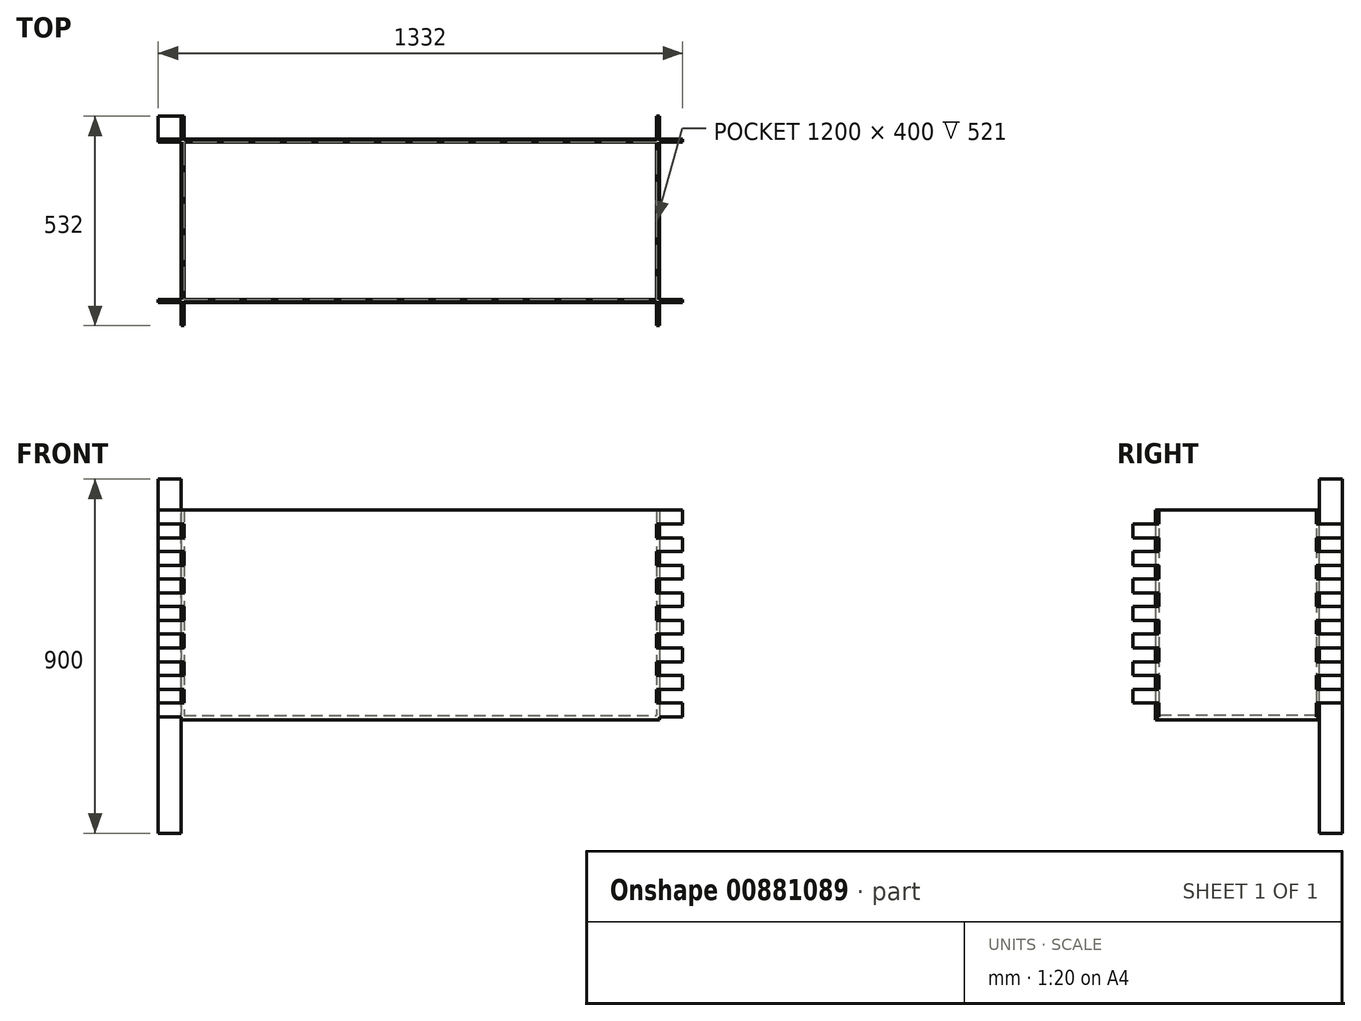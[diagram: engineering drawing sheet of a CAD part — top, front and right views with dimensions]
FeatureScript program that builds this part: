
annotation { "Feature Type Name" : "Feature", "Feature Type Description" : "" }
export const myFeature = defineFeature(function(context is Context, id is Id, definition is map)
    precondition{}
    {
        {
            var Q0;
            Q0=qCreatedBy(makeId("Front.planeOp"),FACE);
            var sketch = newSketch(context, id + "F0", { "sketchPlane" : qUnion([Q0])});
            skLineSegment(sketch, "E0.bottom", {"start": v(-600, 262.5) * mm, "end": v(600, 262.5) * mm});
            skLineSegment(sketch, "E0.top", {"start": v(-600, -262.5) * mm, "end": v(600, -262.5) * mm});
            skLineSegment(sketch, "E0.left", {"start": v(-600, 227.5) * mm, "end": v(-600, 192.5) * mm});
            skPoint(sketch, "E0.middle", {"position": v(0, 0) * mm});
            skLineSegment(sketch, "E1.bottom", {"start": v(-600, 262.5) * mm, "end": v(-666, 262.5) * mm});
            skLineSegment(sketch, "E1.top", {"start": v(-600, 227.5) * mm, "end": v(-666, 227.5) * mm});
            skLineSegment(sketch, "E1.left", {"start": v(-600, 262.5) * mm, "end": v(-600, 227.5) * mm, "construction": true});
            skLineSegment(sketch, "E1.right", {"start": v(-666, 262.5) * mm, "end": v(-666, 227.5) * mm});
            skLineSegment(sketch, "E2.0.1.0", {"start": v(-666, 192.5) * mm, "end": v(-666, 157.5) * mm});
            skLineSegment(sketch, "E2.0.1.1", {"start": v(-600, 192.5) * mm, "end": v(-666, 192.5) * mm});
            skLineSegment(sketch, "E2.0.1.2", {"start": v(-600, 157.5) * mm, "end": v(-666, 157.5) * mm});
            skLineSegment(sketch, "E2.0.2.0", {"start": v(-666, 122.5) * mm, "end": v(-666, 87.5) * mm});
            skLineSegment(sketch, "E2.0.2.1", {"start": v(-600, 122.5) * mm, "end": v(-666, 122.5) * mm});
            skLineSegment(sketch, "E2.0.2.2", {"start": v(-600, 87.5) * mm, "end": v(-666, 87.5) * mm});
            skLineSegment(sketch, "E2.0.3.0", {"start": v(-666, 52.5) * mm, "end": v(-666, 17.5) * mm});
            skLineSegment(sketch, "E2.0.3.1", {"start": v(-600, 52.5) * mm, "end": v(-666, 52.5) * mm});
            skLineSegment(sketch, "E2.0.3.2", {"start": v(-600, 17.5) * mm, "end": v(-666, 17.5) * mm});
            skLineSegment(sketch, "E2.direction1", {"start": v(-666, 227.5) * mm, "end": v(-600, 227.5) * mm, "construction": true});
            skLineSegment(sketch, "E2.direction2", {"start": v(-666, 227.5) * mm, "end": v(-666, 157.5) * mm, "construction": true});
            skLineSegment(sketch, "E3.trimOffspring", {"start": v(-600, 87.5) * mm, "end": v(-600, 52.5) * mm});
            skLineSegment(sketch, "E4.trimOffspring", {"start": v(-600, 157.5) * mm, "end": v(-600, 122.5) * mm});
            skLineSegment(sketch, "E5.0.0.4", {"start": v(-666, -17.5) * mm, "end": v(-666, -52.5) * mm});
            skLineSegment(sketch, "E5.3.0.4", {"start": v(-600, -17.5) * mm, "end": v(-666, -17.5) * mm});
            skLineSegment(sketch, "E5.6.0.4", {"start": v(-600, -52.5) * mm, "end": v(-666, -52.5) * mm});
            skLineSegment(sketch, "E5.0.0.5", {"start": v(-666, -87.5) * mm, "end": v(-666, -122.5) * mm});
            skLineSegment(sketch, "E5.3.0.5", {"start": v(-600, -87.5) * mm, "end": v(-666, -87.5) * mm});
            skLineSegment(sketch, "E5.6.0.5", {"start": v(-600, -122.5) * mm, "end": v(-666, -122.5) * mm});
            skLineSegment(sketch, "E5.0.0.6", {"start": v(-666, -157.5) * mm, "end": v(-666, -192.5) * mm});
            skLineSegment(sketch, "E5.3.0.6", {"start": v(-600, -157.5) * mm, "end": v(-666, -157.5) * mm});
            skLineSegment(sketch, "E5.6.0.6", {"start": v(-600, -192.5) * mm, "end": v(-666, -192.5) * mm});
            skLineSegment(sketch, "E6", {"start": v(-600, 17.5) * mm, "end": v(-600, -17.5) * mm});
            skLineSegment(sketch, "E7", {"start": v(-600, -52.5) * mm, "end": v(-600, -87.5) * mm});
            skLineSegment(sketch, "E8", {"start": v(-600, -122.5) * mm, "end": v(-600, -157.5) * mm});
            skLineSegment(sketch, "E9.MirrorCS", {"start": v(600, -192.5) * mm, "end": v(666, -192.5) * mm});
            skLineSegment(sketch, "E10.MirrorCS", {"start": v(600, 262.5) * mm, "end": v(666, 262.5) * mm});
            skLineSegment(sketch, "E11.MirrorCS", {"start": v(600, 262.5) * mm, "end": v(600, 227.5) * mm, "construction": true});
            skLineSegment(sketch, "E12.MirrorCS", {"start": v(600, 17.5) * mm, "end": v(600, -17.5) * mm});
            skLineSegment(sketch, "E13.MirrorCS", {"start": v(600, 87.5) * mm, "end": v(600, 52.5) * mm});
            skLineSegment(sketch, "E14.MirrorCS", {"start": v(600, -122.5) * mm, "end": v(600, -157.5) * mm});
            skLineSegment(sketch, "E15.MirrorCS", {"start": v(600, 157.5) * mm, "end": v(600, 122.5) * mm});
            skLineSegment(sketch, "E16.MirrorCS", {"start": v(600, 227.5) * mm, "end": v(600, 192.5) * mm});
            skLineSegment(sketch, "E17.MirrorCS", {"start": v(600, -52.5) * mm, "end": v(600, -87.5) * mm});
            skLineSegment(sketch, "E18.MirrorCS", {"start": v(600, 227.5) * mm, "end": v(666, 227.5) * mm});
            skLineSegment(sketch, "E19.MirrorCS", {"start": v(600, -17.5) * mm, "end": v(666, -17.5) * mm});
            skLineSegment(sketch, "E20.MirrorCS", {"start": v(600, 157.5) * mm, "end": v(666, 157.5) * mm});
            skLineSegment(sketch, "E21.MirrorCS", {"start": v(600, 87.5) * mm, "end": v(666, 87.5) * mm});
            skLineSegment(sketch, "E22.MirrorCS", {"start": v(600, 17.5) * mm, "end": v(666, 17.5) * mm});
            skLineSegment(sketch, "E23.MirrorCS", {"start": v(666, 227.5) * mm, "end": v(666, 157.5) * mm, "construction": true});
            skLineSegment(sketch, "E24.MirrorCS", {"start": v(666, 227.5) * mm, "end": v(600, 227.5) * mm, "construction": true});
            skLineSegment(sketch, "E25.MirrorCS", {"start": v(600, -87.5) * mm, "end": v(666, -87.5) * mm});
            skLineSegment(sketch, "E26.MirrorCS", {"start": v(600, -122.5) * mm, "end": v(666, -122.5) * mm});
            skLineSegment(sketch, "E27.MirrorCS", {"start": v(600, -52.5) * mm, "end": v(666, -52.5) * mm});
            skLineSegment(sketch, "E28.MirrorCS", {"start": v(600, 192.5) * mm, "end": v(666, 192.5) * mm});
            skLineSegment(sketch, "E29.MirrorCS", {"start": v(600, 52.5) * mm, "end": v(666, 52.5) * mm});
            skLineSegment(sketch, "E30.MirrorCS", {"start": v(600, -157.5) * mm, "end": v(666, -157.5) * mm});
            skLineSegment(sketch, "E31.MirrorCS", {"start": v(600, 122.5) * mm, "end": v(666, 122.5) * mm});
            skLineSegment(sketch, "E32.MirrorCS", {"start": v(666, -17.5) * mm, "end": v(666, -52.5) * mm});
            skLineSegment(sketch, "E33.MirrorCS", {"start": v(666, -87.5) * mm, "end": v(666, -122.5) * mm});
            skLineSegment(sketch, "E34.MirrorCS", {"start": v(666, 262.5) * mm, "end": v(666, 227.5) * mm});
            skLineSegment(sketch, "E35.MirrorCS", {"start": v(666, 122.5) * mm, "end": v(666, 87.5) * mm});
            skLineSegment(sketch, "E36.MirrorCS", {"start": v(666, 192.5) * mm, "end": v(666, 157.5) * mm});
            skLineSegment(sketch, "E37.MirrorCS", {"start": v(666, -157.5) * mm, "end": v(666, -192.5) * mm});
            skLineSegment(sketch, "E38.MirrorCS", {"start": v(666, 52.5) * mm, "end": v(666, 17.5) * mm});
            skLineSegment(sketch, "E39.0.0.7", {"start": v(-666, -227.5) * mm, "end": v(-666, -262.5) * mm});
            skLineSegment(sketch, "E39.3.0.7", {"start": v(-600, -227.5) * mm, "end": v(-666, -227.5) * mm});
            skLineSegment(sketch, "E39.6.0.7", {"start": v(-600, -262.5) * mm, "end": v(-666, -262.5) * mm});
            skLineSegment(sketch, "E40", {"start": v(-600, -192.5) * mm, "end": v(-600, -227.5) * mm});
            skLineSegment(sketch, "E41.MirrorCS", {"start": v(600, -262.5) * mm, "end": v(666, -262.5) * mm});
            skLineSegment(sketch, "E42.MirrorCS", {"start": v(666, -227.5) * mm, "end": v(666, -262.5) * mm});
            skLineSegment(sketch, "E43.MirrorCS", {"start": v(600, -227.5) * mm, "end": v(666, -227.5) * mm});
            skLineSegment(sketch, "E44.MirrorCS", {"start": v(600, -192.5) * mm, "end": v(600, -227.5) * mm});
            skSolve(sketch);
        }
        {
            var Q0;
            Q0 = qSketchRegion(id + "F0", true);
            extrude(context, id + "F1", {"entities" : qUnion([Q0]), "depth" : 8 * mm, "offsetDistance" : 25 * mm});
        }
        {
            var Q0;
            Q0=makeQuery(id+"F1.opExtrude","SWEPT_FACE",FACE,{"disambiguationData":[OSD([sQuery(id+"F0.wireOp",EDGE,"E0.left")])]});
            var sketch = newSketch(context, id + "F2", { "sketchPlane" : qUnion([Q0])});
            skLineSegment(sketch, "E45.bottom", {"start": v(0, 262.5) * mm, "end": v(-200, 262.5) * mm});
            skLineSegment(sketch, "E45.top", {"start": v(0, -262.5) * mm, "end": v(-200, -262.5) * mm});
            skLineSegment(sketch, "E45.right", {"start": v(-200, 262.5) * mm, "end": v(-200, -262.5) * mm, "construction": true});
            skLineSegment(sketch, "E46.bottom", {"start": v(0, 227.5) * mm, "end": v(66, 227.5) * mm});
            skLineSegment(sketch, "E46.top", {"start": v(0, 192.5) * mm, "end": v(66, 192.5) * mm});
            skLineSegment(sketch, "E46.left", {"start": v(0, 227.5) * mm, "end": v(0, 192.5) * mm, "construction": true});
            skLineSegment(sketch, "E46.right", {"start": v(66, 227.5) * mm, "end": v(66, 192.5) * mm});
            skLineSegment(sketch, "E47.0.1.0", {"start": v(66, 157.5) * mm, "end": v(66, 122.5) * mm});
            skLineSegment(sketch, "E47.0.1.1", {"start": v(0, 157.5) * mm, "end": v(66, 157.5) * mm});
            skLineSegment(sketch, "E47.0.1.2", {"start": v(0, 122.5) * mm, "end": v(66, 122.5) * mm});
            skLineSegment(sketch, "E47.0.2.0", {"start": v(66, 87.5) * mm, "end": v(66, 52.5) * mm});
            skLineSegment(sketch, "E47.0.2.1", {"start": v(0, 87.5) * mm, "end": v(66, 87.5) * mm});
            skLineSegment(sketch, "E47.0.2.2", {"start": v(0, 52.5) * mm, "end": v(66, 52.5) * mm});
            skLineSegment(sketch, "E47.0.3.0", {"start": v(66, 17.5) * mm, "end": v(66, -17.5) * mm});
            skLineSegment(sketch, "E47.0.3.1", {"start": v(0, 17.5) * mm, "end": v(66, 17.5) * mm});
            skLineSegment(sketch, "E47.0.3.2", {"start": v(0, -17.5) * mm, "end": v(66, -17.5) * mm});
            skLineSegment(sketch, "E47.0.4.0", {"start": v(66, -52.5) * mm, "end": v(66, -87.5) * mm});
            skLineSegment(sketch, "E47.0.4.1", {"start": v(0, -52.5) * mm, "end": v(66, -52.5) * mm});
            skLineSegment(sketch, "E47.0.4.2", {"start": v(0, -87.5) * mm, "end": v(66, -87.5) * mm});
            skLineSegment(sketch, "E47.0.5.0", {"start": v(66, -122.5) * mm, "end": v(66, -157.5) * mm});
            skLineSegment(sketch, "E47.0.5.1", {"start": v(0, -122.5) * mm, "end": v(66, -122.5) * mm});
            skLineSegment(sketch, "E47.0.5.2", {"start": v(0, -157.5) * mm, "end": v(66, -157.5) * mm});
            skLineSegment(sketch, "E47.0.6.0", {"start": v(66, -192.5) * mm, "end": v(66, -227.5) * mm});
            skLineSegment(sketch, "E47.0.6.1", {"start": v(0, -192.5) * mm, "end": v(66, -192.5) * mm});
            skLineSegment(sketch, "E47.0.6.2", {"start": v(0, -227.5) * mm, "end": v(66, -227.5) * mm});
            skLineSegment(sketch, "E47.direction1", {"start": v(0, 192.5) * mm, "end": v(25, 192.5) * mm, "construction": true});
            skLineSegment(sketch, "E47.direction2", {"start": v(0, 192.5) * mm, "end": v(0, 157.5) * mm, "construction": true});
            skLineSegment(sketch, "E48.trimOffspring", {"start": v(0, -227.5) * mm, "end": v(0, -262.5) * mm});
            skLineSegment(sketch, "E49.trimOffspring", {"start": v(0, -157.5) * mm, "end": v(0, -192.5) * mm});
            skLineSegment(sketch, "E50.trimOffspring", {"start": v(0, -87.5) * mm, "end": v(0, -122.5) * mm});
            skLineSegment(sketch, "E51.trimOffspring", {"start": v(0, -17.5) * mm, "end": v(0, -52.5) * mm});
            skLineSegment(sketch, "E52.trimOffspring", {"start": v(0, 52.5) * mm, "end": v(0, 17.5) * mm});
            skLineSegment(sketch, "E53.MirrorCS", {"start": v(-400, -17.5) * mm, "end": v(-400, -52.5) * mm});
            skLineSegment(sketch, "E54.MirrorCS", {"start": v(-466, 157.5) * mm, "end": v(-466, 122.5) * mm});
            skLineSegment(sketch, "E55.MirrorCS", {"start": v(-400, 52.5) * mm, "end": v(-400, 17.5) * mm});
            skLineSegment(sketch, "E56.MirrorCS", {"start": v(-400, -157.5) * mm, "end": v(-400, -192.5) * mm});
            skLineSegment(sketch, "E57.MirrorCS", {"start": v(-400, -227.5) * mm, "end": v(-400, -262.5) * mm});
            skLineSegment(sketch, "E58.MirrorCS", {"start": v(-400, -87.5) * mm, "end": v(-400, -122.5) * mm});
            skLineSegment(sketch, "E59.MirrorCS", {"start": v(-466, -52.5) * mm, "end": v(-466, -87.5) * mm});
            skLineSegment(sketch, "E60.MirrorCS", {"start": v(-400, 192.5) * mm, "end": v(-425, 192.5) * mm, "construction": true});
            skLineSegment(sketch, "E61.MirrorCS", {"start": v(-400, 192.5) * mm, "end": v(-400, 157.5) * mm, "construction": true});
            skLineSegment(sketch, "E62.MirrorCS", {"start": v(-466, -122.5) * mm, "end": v(-466, -157.5) * mm});
            skLineSegment(sketch, "E63.MirrorCS", {"start": v(-466, 227.5) * mm, "end": v(-466, 192.5) * mm});
            skLineSegment(sketch, "E64.MirrorCS", {"start": v(-466, 17.5) * mm, "end": v(-466, -17.5) * mm});
            skLineSegment(sketch, "E65.MirrorCS", {"start": v(-400, 227.5) * mm, "end": v(-466, 227.5) * mm});
            skLineSegment(sketch, "E66.MirrorCS", {"start": v(-400, 87.5) * mm, "end": v(-466, 87.5) * mm});
            skLineSegment(sketch, "E67.MirrorCS", {"start": v(-400, -52.5) * mm, "end": v(-466, -52.5) * mm});
            skLineSegment(sketch, "E68.MirrorCS", {"start": v(-400, -157.5) * mm, "end": v(-466, -157.5) * mm});
            skLineSegment(sketch, "E69.MirrorCS", {"start": v(-466, 87.5) * mm, "end": v(-466, 52.5) * mm});
            skLineSegment(sketch, "E70.MirrorCS", {"start": v(-400, -262.5) * mm, "end": v(-200, -262.5) * mm});
            skLineSegment(sketch, "E71.MirrorCS", {"start": v(-400, -122.5) * mm, "end": v(-466, -122.5) * mm});
            skLineSegment(sketch, "E72.MirrorCS", {"start": v(-400, -192.5) * mm, "end": v(-466, -192.5) * mm});
            skLineSegment(sketch, "E73.MirrorCS", {"start": v(-400, 262.5) * mm, "end": v(-200, 262.5) * mm});
            skLineSegment(sketch, "E74.MirrorCS", {"start": v(-400, 192.5) * mm, "end": v(-466, 192.5) * mm});
            skLineSegment(sketch, "E75.MirrorCS", {"start": v(-400, 52.5) * mm, "end": v(-466, 52.5) * mm});
            skLineSegment(sketch, "E76.MirrorCS", {"start": v(-466, -192.5) * mm, "end": v(-466, -227.5) * mm});
            skLineSegment(sketch, "E77.MirrorCS", {"start": v(-400, -227.5) * mm, "end": v(-466, -227.5) * mm});
            skLineSegment(sketch, "E78.MirrorCS", {"start": v(-400, 122.5) * mm, "end": v(-466, 122.5) * mm});
            skLineSegment(sketch, "E79.MirrorCS", {"start": v(-400, 17.5) * mm, "end": v(-466, 17.5) * mm});
            skLineSegment(sketch, "E80.MirrorCS", {"start": v(-400, -87.5) * mm, "end": v(-466, -87.5) * mm});
            skLineSegment(sketch, "E81.MirrorCS", {"start": v(-400, -17.5) * mm, "end": v(-466, -17.5) * mm});
            skLineSegment(sketch, "E82.MirrorCS", {"start": v(-400, 157.5) * mm, "end": v(-466, 157.5) * mm});
            skLineSegment(sketch, "E83", {"start": v(0, 262.5) * mm, "end": v(0, 227.5) * mm});
            skLineSegment(sketch, "E84", {"start": v(-400, 262.5) * mm, "end": v(-400, 227.5) * mm});
            skLineSegment(sketch, "E85", {"start": v(-400, 192.5) * mm, "end": v(-400, 157.5) * mm});
            skLineSegment(sketch, "E86", {"start": v(-400, 122.5) * mm, "end": v(-400, 87.5) * mm});
            skLineSegment(sketch, "E87", {"start": v(0, 192.5) * mm, "end": v(0, 157.5) * mm});
            skLineSegment(sketch, "E88", {"start": v(0, 122.5) * mm, "end": v(0, 87.5) * mm});
            skSolve(sketch);
        }
        {
            var Q0;
            Q0 = qSketchRegion(id + "F2", true);
            extrude(context, id + "F3", {"entities" : qUnion([Q0]), "depth" : 8 * mm, "offsetDistance" : 25 * mm});
        }
        {
            var Q0;
            Q0=makeQuery(id+"F1.opExtrude","SWEPT_BODY",BODY,{"disambiguationData":[OSD([sQuery(id+"F0.wireOp",EDGE,"E0.bottom"),sQuery(id+"F0.wireOp",EDGE,"E0.top"),sQuery(id+"F0.wireOp",EDGE,"E0.left"),sQuery(id+"F0.wireOp",EDGE,"E0.right"),sQuery(id+"F0.wireOp",EDGE,"E1.bottom"),sQuery(id+"F0.wireOp",EDGE,"E1.top"),sQuery(id+"F0.wireOp",EDGE,"E1.right"),sQuery(id+"F0.wireOp",EDGE,"E2.0.1.0"),sQuery(id+"F0.wireOp",EDGE,"E2.0.1.1"),sQuery(id+"F0.wireOp",EDGE,"E2.0.1.2"),sQuery(id+"F0.wireOp",EDGE,"E2.0.2.0"),sQuery(id+"F0.wireOp",EDGE,"E2.0.2.1"),sQuery(id+"F0.wireOp",EDGE,"E2.0.2.2"),sQuery(id+"F0.wireOp",EDGE,"E2.0.3.0"),sQuery(id+"F0.wireOp",EDGE,"E2.0.3.1"),sQuery(id+"F0.wireOp",EDGE,"E2.0.3.2"),sQuery(id+"F0.wireOp",EDGE,"E3.trimOffspring"),sQuery(id+"F0.wireOp",EDGE,"E4.trimOffspring"),sQuery(id+"F0.wireOp",EDGE,"654a2f8d-9041-4c8a-b6f3-2d41a767b8970.MirrorCS"),sQuery(id+"F0.wireOp",EDGE,"654a2f8d-9041-4c8a-b6f3-2d41a767b8973.MirrorCS"),sQuery(id+"F0.wireOp",EDGE,"654a2f8d-9041-4c8a-b6f3-2d41a767b8974.MirrorCS"),sQuery(id+"F0.wireOp",EDGE,"654a2f8d-9041-4c8a-b6f3-2d41a767b8975.MirrorCS"),sQuery(id+"F0.wireOp",EDGE,"654a2f8d-9041-4c8a-b6f3-2d41a767b8976.MirrorCS"),sQuery(id+"F0.wireOp",EDGE,"654a2f8d-9041-4c8a-b6f3-2d41a767b8977.MirrorCS"),sQuery(id+"F0.wireOp",EDGE,"654a2f8d-9041-4c8a-b6f3-2d41a767b8978.MirrorCS"),sQuery(id+"F0.wireOp",EDGE,"654a2f8d-9041-4c8a-b6f3-2d41a767b8979.MirrorCS"),sQuery(id+"F0.wireOp",EDGE,"654a2f8d-9041-4c8a-b6f3-2d41a767b89710.MirrorCS"),sQuery(id+"F0.wireOp",EDGE,"654a2f8d-9041-4c8a-b6f3-2d41a767b89711.MirrorCS"),sQuery(id+"F0.wireOp",EDGE,"654a2f8d-9041-4c8a-b6f3-2d41a767b89712.MirrorCS"),sQuery(id+"F0.wireOp",EDGE,"654a2f8d-9041-4c8a-b6f3-2d41a767b89713.MirrorCS"),sQuery(id+"F0.wireOp",EDGE,"bc8bf7c9-21a7-4010-bfce-5f4c4d057a0e.trimOffspring"),sQuery(id+"F0.wireOp",EDGE,"681b92e8-f1d6-4e1d-b0cf-531c4123ef25.trimOffspring")])]});
            var Q1;
            Q1=makeQuery(id+"F3.opExtrude","CAP_EDGE",EDGE,{"disambiguationData":[OSD([sQuery(id+"F2.wireOp",EDGE,"E45.bottom"),sQuery(id+"F2.wireOp",EDGE,"47e2e538-1496-4ea3-b9ef-a4fa9e4231cb12.MirrorCS")])],"isStart":true});
            var Q2;
            Q2=makeQuery(id+"F3.opExtrude","CAP_EDGE",EDGE,{"disambiguationData":[OSD([sQuery(id+"F2.wireOp",EDGE,"E45.bottom"),sQuery(id+"F2.wireOp",EDGE,"47e2e538-1496-4ea3-b9ef-a4fa9e4231cb12.MirrorCS")])],"isStart":true});
            transform(context, id + "F4", {"entities" : qUnion([Q0]), "transformType" : TransformType.TRANSLATION_DISTANCE, "transformDirection" : qUnion([Q2]), "distance" : 408 * mm, "makeCopy" : true});
        }
        {
            var Q0;
            Q0=makeQuery(id+"F3.opExtrude","SWEPT_BODY",BODY,{"disambiguationData":[OSD([sQuery(id+"F2.wireOp",EDGE,"E45.bottom"),sQuery(id+"F2.wireOp",EDGE,"E45.top"),sQuery(id+"F2.wireOp",EDGE,"E45.left"),sQuery(id+"F2.wireOp",EDGE,"VXF1F787-3TvO-9pyk-sDkr-mCE38lxiraYs.bottom"),sQuery(id+"F2.wireOp",EDGE,"VXF1F787-3TvO-9pyk-sDkr-mCE38lxiraYs.top"),sQuery(id+"F2.wireOp",EDGE,"VXF1F787-3TvO-9pyk-sDkr-mCE38lxiraYs.right"),sQuery(id+"F2.wireOp",EDGE,"92c54758-7377-47f4-830c-e61f3707310f.trimOffspring"),sQuery(id+"F2.wireOp",EDGE,"0bc62775-f8d2-43f3-b865-df8decdc4d50.0.1.0"),sQuery(id+"F2.wireOp",EDGE,"0bc62775-f8d2-43f3-b865-df8decdc4d50.0.1.1"),sQuery(id+"F2.wireOp",EDGE,"0bc62775-f8d2-43f3-b865-df8decdc4d50.0.1.2"),sQuery(id+"F2.wireOp",EDGE,"0bc62775-f8d2-43f3-b865-df8decdc4d50.0.2.0"),sQuery(id+"F2.wireOp",EDGE,"0bc62775-f8d2-43f3-b865-df8decdc4d50.0.2.1"),sQuery(id+"F2.wireOp",EDGE,"0bc62775-f8d2-43f3-b865-df8decdc4d50.0.2.2"),sQuery(id+"F2.wireOp",EDGE,"ff0d782e-37e5-4f16-8f26-1b271ee1eeec.trimOffspring"),sQuery(id+"F2.wireOp",EDGE,"10025bcf-c629-48f1-9c4a-9b3b977cd7b2.trimOffspring"),sQuery(id+"F2.wireOp",EDGE,"47e2e538-1496-4ea3-b9ef-a4fa9e4231cb0.MirrorCS"),sQuery(id+"F2.wireOp",EDGE,"47e2e538-1496-4ea3-b9ef-a4fa9e4231cb1.MirrorCS"),sQuery(id+"F2.wireOp",EDGE,"47e2e538-1496-4ea3-b9ef-a4fa9e4231cb2.MirrorCS"),sQuery(id+"F2.wireOp",EDGE,"47e2e538-1496-4ea3-b9ef-a4fa9e4231cb5.MirrorCS"),sQuery(id+"F2.wireOp",EDGE,"47e2e538-1496-4ea3-b9ef-a4fa9e4231cb6.MirrorCS"),sQuery(id+"F2.wireOp",EDGE,"47e2e538-1496-4ea3-b9ef-a4fa9e4231cb7.MirrorCS"),sQuery(id+"F2.wireOp",EDGE,"47e2e538-1496-4ea3-b9ef-a4fa9e4231cb8.MirrorCS"),sQuery(id+"F2.wireOp",EDGE,"47e2e538-1496-4ea3-b9ef-a4fa9e4231cb9.MirrorCS"),sQuery(id+"F2.wireOp",EDGE,"47e2e538-1496-4ea3-b9ef-a4fa9e4231cb10.MirrorCS"),sQuery(id+"F2.wireOp",EDGE,"47e2e538-1496-4ea3-b9ef-a4fa9e4231cb11.MirrorCS"),sQuery(id+"F2.wireOp",EDGE,"47e2e538-1496-4ea3-b9ef-a4fa9e4231cb12.MirrorCS"),sQuery(id+"F2.wireOp",EDGE,"47e2e538-1496-4ea3-b9ef-a4fa9e4231cb13.MirrorCS"),sQuery(id+"F2.wireOp",EDGE,"47e2e538-1496-4ea3-b9ef-a4fa9e4231cb14.MirrorCS"),sQuery(id+"F2.wireOp",EDGE,"47e2e538-1496-4ea3-b9ef-a4fa9e4231cb15.MirrorCS"),sQuery(id+"F2.wireOp",EDGE,"47e2e538-1496-4ea3-b9ef-a4fa9e4231cb16.MirrorCS")])]});
            var Q1;
            Q1=makeQuery(id+"F4.opPattern","COPY",EDGE,{"derivedFrom":makeQuery(id+"F1.opExtrude","CAP_EDGE",EDGE,{"disambiguationData":[OSD([sQuery(id+"F0.wireOp",EDGE,"E0.bottom"),sQuery(id+"F0.wireOp",EDGE,"E1.bottom"),sQuery(id+"F0.wireOp",EDGE,"654a2f8d-9041-4c8a-b6f3-2d41a767b8978.MirrorCS")])],"isStart":false}),"instanceName":"1"});
            var Q2;
            Q2=makeQuery(id+"F4.opPattern","COPY",EDGE,{"derivedFrom":makeQuery(id+"F1.opExtrude","CAP_EDGE",EDGE,{"disambiguationData":[OSD([sQuery(id+"F0.wireOp",EDGE,"E0.bottom"),sQuery(id+"F0.wireOp",EDGE,"E1.bottom"),sQuery(id+"F0.wireOp",EDGE,"654a2f8d-9041-4c8a-b6f3-2d41a767b8978.MirrorCS")])],"isStart":true}),"instanceName":"1"});
            transform(context, id + "F5", {"entities" : qUnion([Q0]), "transformType" : TransformType.TRANSLATION_DISTANCE, "transformDirection" : qUnion([Q2]), "distance" : 1208 * mm, "makeCopy" : true});
        }
        {
            var Q0;
            Q0=makeQuery(id+"F4.opPattern","COPY",BODY,{"derivedFrom":makeQuery(id+"F1.opExtrude","SWEPT_BODY",BODY,{"disambiguationData":[OSD([sQuery(id+"F0.wireOp",EDGE,"E0.bottom"),sQuery(id+"F0.wireOp",EDGE,"E0.top"),sQuery(id+"F0.wireOp",EDGE,"E0.left"),sQuery(id+"F0.wireOp",EDGE,"E1.bottom"),sQuery(id+"F0.wireOp",EDGE,"E1.top"),sQuery(id+"F0.wireOp",EDGE,"E1.right"),sQuery(id+"F0.wireOp",EDGE,"E2.0.1.0"),sQuery(id+"F0.wireOp",EDGE,"E2.0.1.1"),sQuery(id+"F0.wireOp",EDGE,"E2.0.1.2"),sQuery(id+"F0.wireOp",EDGE,"E2.0.2.0"),sQuery(id+"F0.wireOp",EDGE,"E2.0.2.1"),sQuery(id+"F0.wireOp",EDGE,"E2.0.2.2"),sQuery(id+"F0.wireOp",EDGE,"E2.0.3.0"),sQuery(id+"F0.wireOp",EDGE,"E2.0.3.1"),sQuery(id+"F0.wireOp",EDGE,"E2.0.3.2"),sQuery(id+"F0.wireOp",EDGE,"E3.trimOffspring"),sQuery(id+"F0.wireOp",EDGE,"E4.trimOffspring"),sQuery(id+"F0.wireOp",EDGE,"E5.0.0.4"),sQuery(id+"F0.wireOp",EDGE,"E5.3.0.4"),sQuery(id+"F0.wireOp",EDGE,"E5.6.0.4"),sQuery(id+"F0.wireOp",EDGE,"E5.0.0.5"),sQuery(id+"F0.wireOp",EDGE,"E5.3.0.5"),sQuery(id+"F0.wireOp",EDGE,"E5.6.0.5"),sQuery(id+"F0.wireOp",EDGE,"E5.0.0.6"),sQuery(id+"F0.wireOp",EDGE,"E5.3.0.6"),sQuery(id+"F0.wireOp",EDGE,"E5.6.0.6"),sQuery(id+"F0.wireOp",EDGE,"E6"),sQuery(id+"F0.wireOp",EDGE,"E7"),sQuery(id+"F0.wireOp",EDGE,"E8"),sQuery(id+"F0.wireOp",EDGE,"E9.MirrorCS"),sQuery(id+"F0.wireOp",EDGE,"E10.MirrorCS"),sQuery(id+"F0.wireOp",EDGE,"E12.MirrorCS"),sQuery(id+"F0.wireOp",EDGE,"E13.MirrorCS"),sQuery(id+"F0.wireOp",EDGE,"E14.MirrorCS"),sQuery(id+"F0.wireOp",EDGE,"E15.MirrorCS"),sQuery(id+"F0.wireOp",EDGE,"E16.MirrorCS"),sQuery(id+"F0.wireOp",EDGE,"E17.MirrorCS"),sQuery(id+"F0.wireOp",EDGE,"E18.MirrorCS"),sQuery(id+"F0.wireOp",EDGE,"E19.MirrorCS"),sQuery(id+"F0.wireOp",EDGE,"E20.MirrorCS"),sQuery(id+"F0.wireOp",EDGE,"E21.MirrorCS"),sQuery(id+"F0.wireOp",EDGE,"E22.MirrorCS"),sQuery(id+"F0.wireOp",EDGE,"E25.MirrorCS"),sQuery(id+"F0.wireOp",EDGE,"E26.MirrorCS"),sQuery(id+"F0.wireOp",EDGE,"E27.MirrorCS"),sQuery(id+"F0.wireOp",EDGE,"E28.MirrorCS"),sQuery(id+"F0.wireOp",EDGE,"E29.MirrorCS"),sQuery(id+"F0.wireOp",EDGE,"E30.MirrorCS"),sQuery(id+"F0.wireOp",EDGE,"E31.MirrorCS"),sQuery(id+"F0.wireOp",EDGE,"E32.MirrorCS"),sQuery(id+"F0.wireOp",EDGE,"E33.MirrorCS"),sQuery(id+"F0.wireOp",EDGE,"E34.MirrorCS"),sQuery(id+"F0.wireOp",EDGE,"E35.MirrorCS"),sQuery(id+"F0.wireOp",EDGE,"E36.MirrorCS"),sQuery(id+"F0.wireOp",EDGE,"E37.MirrorCS"),sQuery(id+"F0.wireOp",EDGE,"E38.MirrorCS"),sQuery(id+"F0.wireOp",EDGE,"E39.0.0.7"),sQuery(id+"F0.wireOp",EDGE,"E39.3.0.7"),sQuery(id+"F0.wireOp",EDGE,"E39.6.0.7"),sQuery(id+"F0.wireOp",EDGE,"E40"),sQuery(id+"F0.wireOp",EDGE,"E41.MirrorCS"),sQuery(id+"F0.wireOp",EDGE,"E42.MirrorCS"),sQuery(id+"F0.wireOp",EDGE,"E43.MirrorCS"),sQuery(id+"F0.wireOp",EDGE,"E44.MirrorCS")])]}),"instanceName":"1"});
            deleteBodies(context, id + "F6", {"entities" : qUnion([Q0])});
        }
        {
            var Q0;
            Q0=makeQuery(id+"F5.opPattern","COPY",FACE,{"derivedFrom":makeQuery(id+"F3.opExtrude","SWEPT_FACE",FACE,{"disambiguationData":[OSD([sQuery(id+"F2.wireOp",EDGE,"E84")])]}),"instanceName":"1"});
            var sketch = newSketch(context, id + "F7", { "sketchPlane" : qUnion([Q0])});
            skLineSegment(sketch, "E89.0.0", {"start": v(-666, -262.5) * mm, "end": v(666, -262.5) * mm});
            skLineSegment(sketch, "E89.0.1", {"start": v(666, -262.5) * mm, "end": v(666, -227.5) * mm});
            skLineSegment(sketch, "E89.0.2", {"start": v(666, -227.5) * mm, "end": v(600, -227.5) * mm});
            skLineSegment(sketch, "E89.0.3", {"start": v(600, -227.5) * mm, "end": v(600, -192.5) * mm});
            skLineSegment(sketch, "E89.0.4", {"start": v(600, -192.5) * mm, "end": v(666, -192.5) * mm});
            skLineSegment(sketch, "E89.0.5", {"start": v(666, -192.5) * mm, "end": v(666, -157.5) * mm});
            skLineSegment(sketch, "E89.0.6", {"start": v(666, -157.5) * mm, "end": v(600, -157.5) * mm});
            skLineSegment(sketch, "E89.0.7", {"start": v(600, -157.5) * mm, "end": v(600, -122.5) * mm});
            skLineSegment(sketch, "E89.0.8", {"start": v(600, -122.5) * mm, "end": v(666, -122.5) * mm});
            skLineSegment(sketch, "E89.0.9", {"start": v(666, -122.5) * mm, "end": v(666, -87.5) * mm});
            skLineSegment(sketch, "E89.0.10", {"start": v(666, -87.5) * mm, "end": v(600, -87.5) * mm});
            skLineSegment(sketch, "E89.0.11", {"start": v(600, -87.5) * mm, "end": v(600, -52.5) * mm});
            skLineSegment(sketch, "E89.0.12", {"start": v(600, -52.5) * mm, "end": v(666, -52.5) * mm});
            skLineSegment(sketch, "E89.0.13", {"start": v(666, -52.5) * mm, "end": v(666, -17.5) * mm});
            skLineSegment(sketch, "E89.0.14", {"start": v(666, -17.5) * mm, "end": v(600, -17.5) * mm});
            skLineSegment(sketch, "E89.0.15", {"start": v(600, -17.5) * mm, "end": v(600, 17.5) * mm});
            skLineSegment(sketch, "E89.0.16", {"start": v(600, 17.5) * mm, "end": v(666, 17.5) * mm});
            skLineSegment(sketch, "E89.0.17", {"start": v(666, 17.5) * mm, "end": v(666, 52.5) * mm});
            skLineSegment(sketch, "E89.0.18", {"start": v(666, 52.5) * mm, "end": v(600, 52.5) * mm});
            skLineSegment(sketch, "E89.0.19", {"start": v(600, 52.5) * mm, "end": v(600, 87.5) * mm});
            skLineSegment(sketch, "E89.0.20", {"start": v(600, 87.5) * mm, "end": v(666, 87.5) * mm});
            skLineSegment(sketch, "E89.0.21", {"start": v(666, 87.5) * mm, "end": v(666, 122.5) * mm});
            skLineSegment(sketch, "E89.0.22", {"start": v(666, 122.5) * mm, "end": v(600, 122.5) * mm});
            skLineSegment(sketch, "E89.0.23", {"start": v(600, 122.5) * mm, "end": v(600, 157.5) * mm});
            skLineSegment(sketch, "E89.0.24", {"start": v(600, 157.5) * mm, "end": v(666, 157.5) * mm});
            skLineSegment(sketch, "E89.0.25", {"start": v(666, 157.5) * mm, "end": v(666, 192.5) * mm});
            skLineSegment(sketch, "E89.0.26", {"start": v(666, 192.5) * mm, "end": v(600, 192.5) * mm});
            skLineSegment(sketch, "E89.0.27", {"start": v(600, 192.5) * mm, "end": v(600, 227.5) * mm});
            skLineSegment(sketch, "E89.0.28", {"start": v(600, 227.5) * mm, "end": v(666, 227.5) * mm});
            skLineSegment(sketch, "E89.0.29", {"start": v(666, 227.5) * mm, "end": v(666, 262.5) * mm});
            skLineSegment(sketch, "E89.0.30", {"start": v(666, 262.5) * mm, "end": v(-666, 262.5) * mm});
            skLineSegment(sketch, "E89.0.31", {"start": v(-666, 262.5) * mm, "end": v(-666, 227.5) * mm});
            skLineSegment(sketch, "E89.0.32", {"start": v(-666, 227.5) * mm, "end": v(-600, 227.5) * mm});
            skLineSegment(sketch, "E89.0.33", {"start": v(-600, 227.5) * mm, "end": v(-600, 192.5) * mm});
            skLineSegment(sketch, "E89.0.34", {"start": v(-600, 192.5) * mm, "end": v(-666, 192.5) * mm});
            skLineSegment(sketch, "E89.0.35", {"start": v(-666, 192.5) * mm, "end": v(-666, 157.5) * mm});
            skLineSegment(sketch, "E89.0.36", {"start": v(-666, 157.5) * mm, "end": v(-600, 157.5) * mm});
            skLineSegment(sketch, "E89.0.37", {"start": v(-600, 157.5) * mm, "end": v(-600, 122.5) * mm});
            skLineSegment(sketch, "E89.0.38", {"start": v(-600, 122.5) * mm, "end": v(-666, 122.5) * mm});
            skLineSegment(sketch, "E89.0.39", {"start": v(-666, 122.5) * mm, "end": v(-666, 87.5) * mm});
            skLineSegment(sketch, "E89.0.40", {"start": v(-666, 87.5) * mm, "end": v(-600, 87.5) * mm});
            skLineSegment(sketch, "E89.0.41", {"start": v(-600, 87.5) * mm, "end": v(-600, 52.5) * mm});
            skLineSegment(sketch, "E89.0.42", {"start": v(-600, 52.5) * mm, "end": v(-666, 52.5) * mm});
            skLineSegment(sketch, "E89.0.43", {"start": v(-666, 52.5) * mm, "end": v(-666, 17.5) * mm});
            skLineSegment(sketch, "E89.0.44", {"start": v(-666, 17.5) * mm, "end": v(-600, 17.5) * mm});
            skLineSegment(sketch, "E89.0.45", {"start": v(-600, 17.5) * mm, "end": v(-600, -17.5) * mm});
            skLineSegment(sketch, "E89.0.46", {"start": v(-600, -17.5) * mm, "end": v(-666, -17.5) * mm});
            skLineSegment(sketch, "E89.0.47", {"start": v(-666, -17.5) * mm, "end": v(-666, -52.5) * mm});
            skLineSegment(sketch, "E89.0.48", {"start": v(-666, -52.5) * mm, "end": v(-600, -52.5) * mm});
            skLineSegment(sketch, "E89.0.49", {"start": v(-600, -52.5) * mm, "end": v(-600, -87.5) * mm});
            skLineSegment(sketch, "E89.0.50", {"start": v(-600, -87.5) * mm, "end": v(-666, -87.5) * mm});
            skLineSegment(sketch, "E89.0.51", {"start": v(-666, -87.5) * mm, "end": v(-666, -122.5) * mm});
            skLineSegment(sketch, "E89.0.52", {"start": v(-666, -122.5) * mm, "end": v(-600, -122.5) * mm});
            skLineSegment(sketch, "E89.0.53", {"start": v(-600, -122.5) * mm, "end": v(-600, -157.5) * mm});
            skLineSegment(sketch, "E89.0.54", {"start": v(-600, -157.5) * mm, "end": v(-666, -157.5) * mm});
            skLineSegment(sketch, "E89.0.55", {"start": v(-666, -157.5) * mm, "end": v(-666, -192.5) * mm});
            skLineSegment(sketch, "E89.0.56", {"start": v(-666, -192.5) * mm, "end": v(-600, -192.5) * mm});
            skLineSegment(sketch, "E89.0.57", {"start": v(-600, -192.5) * mm, "end": v(-600, -227.5) * mm});
            skLineSegment(sketch, "E89.0.58", {"start": v(-600, -227.5) * mm, "end": v(-666, -227.5) * mm});
            skLineSegment(sketch, "E89.0.59", {"start": v(-666, -227.5) * mm, "end": v(-666, -262.5) * mm});
            skSolve(sketch);
        }
        {
            var Q0;
            Q0 = qSketchRegion(id + "F7", true);
            extrude(context, id + "F8", {"entities" : qUnion([Q0]), "depth" : 8 * mm, "offsetDistance" : 25 * mm});
        }
        {
            var Q0;
            Q0=makeQuery(id+"F5.opPattern","COPY",BODY,{"derivedFrom":makeQuery(id+"F3.opExtrude","SWEPT_BODY",BODY,{"disambiguationData":[OSD([sQuery(id+"F2.wireOp",EDGE,"E45.bottom"),sQuery(id+"F2.wireOp",EDGE,"E45.top"),sQuery(id+"F2.wireOp",EDGE,"E46.bottom"),sQuery(id+"F2.wireOp",EDGE,"E46.top"),sQuery(id+"F2.wireOp",EDGE,"E46.right"),sQuery(id+"F2.wireOp",EDGE,"E47.0.1.0"),sQuery(id+"F2.wireOp",EDGE,"E47.0.1.1"),sQuery(id+"F2.wireOp",EDGE,"E47.0.1.2"),sQuery(id+"F2.wireOp",EDGE,"E47.0.2.0"),sQuery(id+"F2.wireOp",EDGE,"E47.0.2.1"),sQuery(id+"F2.wireOp",EDGE,"E47.0.2.2"),sQuery(id+"F2.wireOp",EDGE,"E47.0.3.0"),sQuery(id+"F2.wireOp",EDGE,"E47.0.3.1"),sQuery(id+"F2.wireOp",EDGE,"E47.0.3.2"),sQuery(id+"F2.wireOp",EDGE,"E47.0.4.0"),sQuery(id+"F2.wireOp",EDGE,"E47.0.4.1"),sQuery(id+"F2.wireOp",EDGE,"E47.0.4.2"),sQuery(id+"F2.wireOp",EDGE,"E47.0.5.0"),sQuery(id+"F2.wireOp",EDGE,"E47.0.5.1"),sQuery(id+"F2.wireOp",EDGE,"E47.0.5.2"),sQuery(id+"F2.wireOp",EDGE,"E47.0.6.0"),sQuery(id+"F2.wireOp",EDGE,"E47.0.6.1"),sQuery(id+"F2.wireOp",EDGE,"E47.0.6.2"),sQuery(id+"F2.wireOp",EDGE,"E48.trimOffspring"),sQuery(id+"F2.wireOp",EDGE,"E49.trimOffspring"),sQuery(id+"F2.wireOp",EDGE,"E50.trimOffspring"),sQuery(id+"F2.wireOp",EDGE,"E51.trimOffspring"),sQuery(id+"F2.wireOp",EDGE,"E52.trimOffspring"),sQuery(id+"F2.wireOp",EDGE,"E53.MirrorCS"),sQuery(id+"F2.wireOp",EDGE,"E54.MirrorCS"),sQuery(id+"F2.wireOp",EDGE,"E55.MirrorCS"),sQuery(id+"F2.wireOp",EDGE,"E56.MirrorCS"),sQuery(id+"F2.wireOp",EDGE,"E57.MirrorCS"),sQuery(id+"F2.wireOp",EDGE,"E58.MirrorCS"),sQuery(id+"F2.wireOp",EDGE,"E59.MirrorCS"),sQuery(id+"F2.wireOp",EDGE,"E62.MirrorCS"),sQuery(id+"F2.wireOp",EDGE,"E63.MirrorCS"),sQuery(id+"F2.wireOp",EDGE,"E64.MirrorCS"),sQuery(id+"F2.wireOp",EDGE,"E65.MirrorCS"),sQuery(id+"F2.wireOp",EDGE,"E66.MirrorCS"),sQuery(id+"F2.wireOp",EDGE,"E67.MirrorCS"),sQuery(id+"F2.wireOp",EDGE,"E68.MirrorCS"),sQuery(id+"F2.wireOp",EDGE,"E69.MirrorCS"),sQuery(id+"F2.wireOp",EDGE,"E70.MirrorCS"),sQuery(id+"F2.wireOp",EDGE,"E71.MirrorCS"),sQuery(id+"F2.wireOp",EDGE,"E72.MirrorCS"),sQuery(id+"F2.wireOp",EDGE,"E73.MirrorCS"),sQuery(id+"F2.wireOp",EDGE,"E74.MirrorCS"),sQuery(id+"F2.wireOp",EDGE,"E75.MirrorCS"),sQuery(id+"F2.wireOp",EDGE,"E76.MirrorCS"),sQuery(id+"F2.wireOp",EDGE,"E77.MirrorCS"),sQuery(id+"F2.wireOp",EDGE,"E78.MirrorCS"),sQuery(id+"F2.wireOp",EDGE,"E79.MirrorCS"),sQuery(id+"F2.wireOp",EDGE,"E80.MirrorCS"),sQuery(id+"F2.wireOp",EDGE,"E81.MirrorCS"),sQuery(id+"F2.wireOp",EDGE,"E82.MirrorCS"),sQuery(id+"F2.wireOp",EDGE,"E83"),sQuery(id+"F2.wireOp",EDGE,"E84"),sQuery(id+"F2.wireOp",EDGE,"E85"),sQuery(id+"F2.wireOp",EDGE,"E86"),sQuery(id+"F2.wireOp",EDGE,"E87"),sQuery(id+"F2.wireOp",EDGE,"E88")])]}),"instanceName":"1"});
            deleteBodies(context, id + "F9", {"entities" : qUnion([Q0])});
        }
        {
            var Q0;
            Q0=makeQuery(id+"F8.opExtrude","SWEPT_FACE",FACE,{"disambiguationData":[OSD([sQuery(id+"F7.wireOp",EDGE,"E89.0.49")])]});
            var sketch = newSketch(context, id + "F10", { "sketchPlane" : qUnion([Q0])});
            skLineSegment(sketch, "E90.0.0", {"start": v(0, 192.5) * mm, "end": v(0, 157.5) * mm});
            skLineSegment(sketch, "E90.0.1", {"start": v(0, 157.5) * mm, "end": v(-66, 157.5) * mm});
            skLineSegment(sketch, "E90.0.2", {"start": v(-66, 157.5) * mm, "end": v(-66, 122.5) * mm});
            skLineSegment(sketch, "E90.0.3", {"start": v(-66, 122.5) * mm, "end": v(0, 122.5) * mm});
            skLineSegment(sketch, "E90.0.4", {"start": v(0, 122.5) * mm, "end": v(0, 87.5) * mm});
            skLineSegment(sketch, "E90.0.5", {"start": v(0, 87.5) * mm, "end": v(-66, 87.5) * mm});
            skLineSegment(sketch, "E90.0.6", {"start": v(-66, 87.5) * mm, "end": v(-66, 52.5) * mm});
            skLineSegment(sketch, "E90.0.7", {"start": v(-66, 52.5) * mm, "end": v(0, 52.5) * mm});
            skLineSegment(sketch, "E90.0.8", {"start": v(0, 52.5) * mm, "end": v(0, 17.5) * mm});
            skLineSegment(sketch, "E90.0.9", {"start": v(0, 17.5) * mm, "end": v(-66, 17.5) * mm});
            skLineSegment(sketch, "E90.0.10", {"start": v(-66, 17.5) * mm, "end": v(-66, -17.5) * mm});
            skLineSegment(sketch, "E90.0.11", {"start": v(-66, -17.5) * mm, "end": v(0, -17.5) * mm});
            skLineSegment(sketch, "E90.0.12", {"start": v(0, -17.5) * mm, "end": v(0, -52.5) * mm});
            skLineSegment(sketch, "E90.0.13", {"start": v(0, -52.5) * mm, "end": v(-66, -52.5) * mm});
            skLineSegment(sketch, "E90.0.14", {"start": v(-66, -52.5) * mm, "end": v(-66, -87.5) * mm});
            skLineSegment(sketch, "E90.0.15", {"start": v(-66, -87.5) * mm, "end": v(0, -87.5) * mm});
            skLineSegment(sketch, "E90.0.16", {"start": v(0, -87.5) * mm, "end": v(0, -122.5) * mm});
            skLineSegment(sketch, "E90.0.17", {"start": v(0, -122.5) * mm, "end": v(-66, -122.5) * mm});
            skLineSegment(sketch, "E90.0.18", {"start": v(-66, -122.5) * mm, "end": v(-66, -157.5) * mm});
            skLineSegment(sketch, "E90.0.19", {"start": v(-66, -157.5) * mm, "end": v(0, -157.5) * mm});
            skLineSegment(sketch, "E90.0.20", {"start": v(0, -157.5) * mm, "end": v(0, -192.5) * mm});
            skLineSegment(sketch, "E90.0.21", {"start": v(0, -192.5) * mm, "end": v(-66, -192.5) * mm});
            skLineSegment(sketch, "E90.0.22", {"start": v(-66, -192.5) * mm, "end": v(-66, -227.5) * mm});
            skLineSegment(sketch, "E90.0.23", {"start": v(-66, -227.5) * mm, "end": v(0, -227.5) * mm});
            skLineSegment(sketch, "E90.0.24", {"start": v(0, -227.5) * mm, "end": v(0, -262.5) * mm});
            skLineSegment(sketch, "E90.0.25", {"start": v(0, -262.5) * mm, "end": v(400, -262.5) * mm});
            skLineSegment(sketch, "E90.0.26", {"start": v(400, -262.5) * mm, "end": v(400, -227.5) * mm});
            skLineSegment(sketch, "E90.0.27", {"start": v(400, -227.5) * mm, "end": v(466, -227.5) * mm});
            skLineSegment(sketch, "E90.0.28", {"start": v(466, -227.5) * mm, "end": v(466, -192.5) * mm});
            skLineSegment(sketch, "E90.0.29", {"start": v(466, -192.5) * mm, "end": v(400, -192.5) * mm});
            skLineSegment(sketch, "E90.0.30", {"start": v(400, -192.5) * mm, "end": v(400, -157.5) * mm});
            skLineSegment(sketch, "E90.0.31", {"start": v(400, -157.5) * mm, "end": v(466, -157.5) * mm});
            skLineSegment(sketch, "E90.0.32", {"start": v(466, -157.5) * mm, "end": v(466, -122.5) * mm});
            skLineSegment(sketch, "E90.0.33", {"start": v(466, -122.5) * mm, "end": v(400, -122.5) * mm});
            skLineSegment(sketch, "E90.0.34", {"start": v(400, -122.5) * mm, "end": v(400, -87.5) * mm});
            skLineSegment(sketch, "E90.0.35", {"start": v(400, -87.5) * mm, "end": v(466, -87.5) * mm});
            skLineSegment(sketch, "E90.0.36", {"start": v(466, -87.5) * mm, "end": v(466, -52.5) * mm});
            skLineSegment(sketch, "E90.0.37", {"start": v(466, -52.5) * mm, "end": v(400, -52.5) * mm});
            skLineSegment(sketch, "E90.0.38", {"start": v(400, -52.5) * mm, "end": v(400, -17.5) * mm});
            skLineSegment(sketch, "E90.0.39", {"start": v(400, -17.5) * mm, "end": v(466, -17.5) * mm});
            skLineSegment(sketch, "E90.0.40", {"start": v(466, -17.5) * mm, "end": v(466, 17.5) * mm});
            skLineSegment(sketch, "E90.0.41", {"start": v(466, 17.5) * mm, "end": v(400, 17.5) * mm});
            skLineSegment(sketch, "E90.0.42", {"start": v(400, 17.5) * mm, "end": v(400, 52.5) * mm});
            skLineSegment(sketch, "E90.0.43", {"start": v(400, 52.5) * mm, "end": v(466, 52.5) * mm});
            skLineSegment(sketch, "E90.0.44", {"start": v(466, 52.5) * mm, "end": v(466, 87.5) * mm});
            skLineSegment(sketch, "E90.0.45", {"start": v(466, 87.5) * mm, "end": v(400, 87.5) * mm});
            skLineSegment(sketch, "E90.0.46", {"start": v(400, 87.5) * mm, "end": v(400, 122.5) * mm});
            skLineSegment(sketch, "E90.0.47", {"start": v(400, 122.5) * mm, "end": v(466, 122.5) * mm});
            skLineSegment(sketch, "E90.0.48", {"start": v(466, 122.5) * mm, "end": v(466, 157.5) * mm});
            skLineSegment(sketch, "E90.0.49", {"start": v(466, 157.5) * mm, "end": v(400, 157.5) * mm});
            skLineSegment(sketch, "E90.0.50", {"start": v(400, 157.5) * mm, "end": v(400, 192.5) * mm});
            skLineSegment(sketch, "E90.0.51", {"start": v(400, 192.5) * mm, "end": v(466, 192.5) * mm});
            skLineSegment(sketch, "E90.0.52", {"start": v(466, 192.5) * mm, "end": v(466, 227.5) * mm});
            skLineSegment(sketch, "E90.0.53", {"start": v(466, 227.5) * mm, "end": v(400, 227.5) * mm});
            skLineSegment(sketch, "E90.0.54", {"start": v(400, 227.5) * mm, "end": v(400, 262.5) * mm});
            skLineSegment(sketch, "E90.0.55", {"start": v(400, 262.5) * mm, "end": v(0, 262.5) * mm});
            skLineSegment(sketch, "E90.0.57", {"start": v(0, 227.5) * mm, "end": v(-66, 227.5) * mm});
            skLineSegment(sketch, "E90.0.58", {"start": v(-66, 227.5) * mm, "end": v(-66, 192.5) * mm});
            skLineSegment(sketch, "E90.0.59", {"start": v(-66, 192.5) * mm, "end": v(0, 192.5) * mm});
            skLineSegment(sketch, "E91", {"start": v(0, 262.5) * mm, "end": v(0, 227.5) * mm});
            skSolve(sketch);
        }
        {
            var Q0;
            Q0 = qSketchRegion(id + "F10", true);
            extrude(context, id + "F11", {"entities" : qUnion([Q0]), "depth" : 8 * mm, "offsetDistance" : 25 * mm});
        }
        {
            var Q0;
            Q0=makeQuery(id+"F1.opExtrude","SWEPT_FACE",FACE,{"disambiguationData":[OSD([sQuery(id+"F0.wireOp",EDGE,"E0.top"),sQuery(id+"F0.wireOp",EDGE,"E39.6.0.7"),sQuery(id+"F0.wireOp",EDGE,"E41.MirrorCS")])]});
            var sketch = newSketch(context, id + "F12", { "sketchPlane" : qUnion([Q0])});
            skLineSegment(sketch, "E92.bottom", {"start": v(608, 8) * mm, "end": v(-608, 8) * mm});
            skLineSegment(sketch, "E92.top", {"start": v(608, -408) * mm, "end": v(-608, -408) * mm});
            skLineSegment(sketch, "E92.left", {"start": v(608, 8) * mm, "end": v(608, -408) * mm});
            skLineSegment(sketch, "E92.right", {"start": v(-608, 8) * mm, "end": v(-608, -408) * mm});
            skSolve(sketch);
        }
        {
            var Q0;
            Q0 = qSketchRegion(id + "F12", true);
            extrude(context, id + "F13", {"entities" : qUnion([Q0]), "depth" : 8 * mm, "offsetDistance" : 25 * mm});
        }
        {
            var Q0;
            Q0=makeQuery(id+"F13.opExtrude","CAP_FACE",FACE,{"disambiguationData":[OSD([sQuery(id+"F12.wireOp",EDGE,"E92.bottom"),sQuery(id+"F12.wireOp",EDGE,"E92.top"),sQuery(id+"F12.wireOp",EDGE,"E92.left"),sQuery(id+"F12.wireOp",EDGE,"E92.right")])],"isStart":true});
            var sketch = newSketch(context, id + "F14", { "sketchPlane" : qUnion([Q0])});
            skLineSegment(sketch, "E93.bottom", {"start": v(-600, 400) * mm, "end": v(600, 400) * mm});
            skLineSegment(sketch, "E93.top", {"start": v(-600, 0) * mm, "end": v(600, 0) * mm});
            skLineSegment(sketch, "E93.left", {"start": v(-600, 400) * mm, "end": v(-600, 0) * mm});
            skLineSegment(sketch, "E93.right", {"start": v(600, 400) * mm, "end": v(600, 0) * mm});
            skSolve(sketch);
        }
        {
            var Q0;
            Q0 = qSketchRegion(id + "F14", true);
            extrude(context, id + "F15", {"entities" : qUnion([Q0]), "operationType" : NewBodyOperationType.ADD, "depth" : 4 * mm, "offsetDistance" : 25 * mm});
        }
        {
            var Q0;
            Q0=makeQuery(id+"F15.opExtrude","CAP_FACE",FACE,{"disambiguationData":[OSD([sQuery(id+"F14.wireOp",EDGE,"E93.bottom"),sQuery(id+"F14.wireOp",EDGE,"E93.top"),sQuery(id+"F14.wireOp",EDGE,"E93.left"),sQuery(id+"F14.wireOp",EDGE,"E93.right")])],"isStart":false});
            cPlane(context, id + "F16", {"entities" : qUnion([Q0]), "cplaneType" : CPlaneType.OFFSET, "offset" : 600 * mm, "width" : 150 * mm, "height" : 150 * mm});
        }
        {
            var Q0;
            Q0=qCreatedBy(id+"F16.planeOp",FACE);
            var sketch = newSketch(context, id + "F17", { "sketchPlane" : qUnion([Q0])});
            skLineSegment(sketch, "E94.bottom", {"start": v(-608, 408) * mm, "end": v(-666, 408) * mm});
            skLineSegment(sketch, "E94.top", {"start": v(-608, 466) * mm, "end": v(-666, 466) * mm});
            skLineSegment(sketch, "E94.left", {"start": v(-608, 408) * mm, "end": v(-608, 466) * mm});
            skLineSegment(sketch, "E94.right", {"start": v(-666, 408) * mm, "end": v(-666, 466) * mm});
            skSolve(sketch);
        }
        {
            var Q0;
            Q0 = qSketchRegion(id + "F17", true);
            extrude(context, id + "F18", {"entities" : qUnion([Q0]), "oppositeDirection" : true, "depth" : 900 * mm, "offsetDistance" : 25 * mm});
        }
    });
